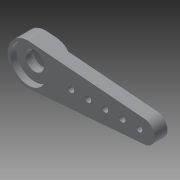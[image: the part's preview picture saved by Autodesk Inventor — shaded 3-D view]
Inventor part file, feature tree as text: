
AUTODESK INVENTOR PART (.ipt)
format: ipt  version: 2015 SP2 (Build 190223200, 223)  size: 147,456 bytes
history: native  units: mm
features: sketch x7, extrude x4, hole x3, fillet x1
ambient origin geometry x8: Origin, YZ Plane, XZ Plane, XY Plane, X Axis, Y Axis, Z Axis, Center Point
bodies: Solid1 (feature_tree)
feature tree (15):
  extrude  "Extrusion1"  Depth=11.314mm
  extrude  "Extrusion2"  Depth=2.5mm
  fillet  "Fillet1"  Radius=36.0mm
  sketch  "Sketch4"  dims[d5=7.0mm d6=4.0mm d7=0.0mm]
  extrude  "Extrusion3"  Depth=4.0mm TaperAngle=0.0deg
  sketch  "Sketch6"  dims[d11=5.8mm d13=0.5mm d14=0.0mm]
  hole  "Hole1"  [1 undecoded]
  hole  "Hole2"  [1 undecoded]
  hole  "Hole4"  [1 undecoded]
  extrude  "Extrusion5"  Depth=0.3mm
  sketch  "Sketch1"  dims[d0=12.9mm d1=11.314mm]
  sketch  "Sketch2"  dims[d2=5.7mm d3=2.5mm d4=36.0mm]
  sketch  "Sketch5"  dims[d8=1.5mm d9=0.0mm d10=10.0mm]
  sketch  "Sketch7"  dims[d15=2.0mm d16=0.0mm d17=5.8mm]
  sketch  "Sketch9"  dims[d20=3.0mm d21=6.0mm d22=4.0mm d23=2.0mm d24=90.0deg d25=8.0mm d26=20.594885mm d27=5.8mm d28=5.8mm d29=6.0mm d30=4.0mm d31=2.0mm d32=90.0deg d33=2.0mm d34=20.594885mm d47=2.0mm d48=6.0mm d49=4.0mm d50=2.0mm d51=90.0deg d52=1.0mm d53=20.594885mm d54=0.3mm d55=0.0mm]
note: 3 required parameter values undecoded (feature->parameter linkage not recoverable at this tier; creation-order binding heuristic only, values carry confidence <= 0.55)
